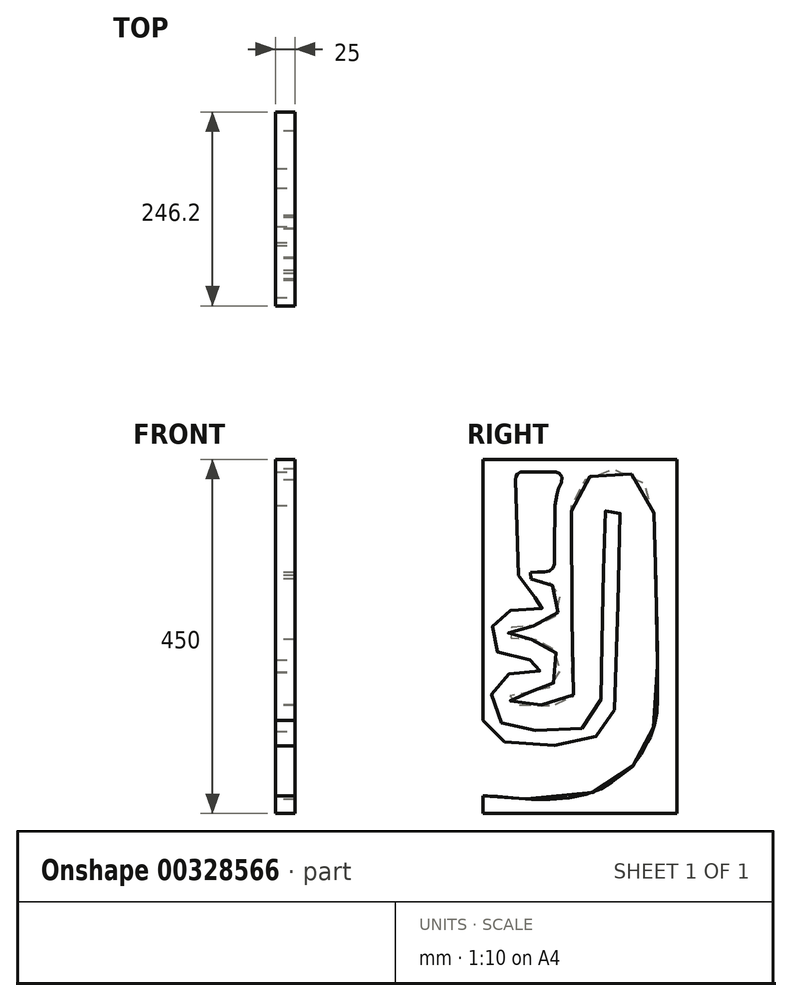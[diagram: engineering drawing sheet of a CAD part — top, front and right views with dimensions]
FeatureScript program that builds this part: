
annotation { "Feature Type Name" : "Feature", "Feature Type Description" : "" }
export const myFeature = defineFeature(function(context is Context, id is Id, definition is map)
    precondition{}
    {
        {
            var Q0;
            Q0=qCreatedBy(makeId("Right.planeOp"),FACE);
            var sketch = newSketch(context, id + "F0", { "sketchPlane" : qUnion([Q0])});
            skLineSegment(sketch, "E0", {"start": v(44.97, 302.71) * mm, "end": v(0, 299.98) * mm, "construction": true});
            skFitSpline(sketch, "E1", {"points": [v(44.97, 302.71) * mm, v(46.66, 291.94) * mm, v(50.27, 282.54) * mm, v(59.09, 276.03) * mm, v(68.36, 274.38) * mm, v(74.74, 273.73) * mm, v(78.42, 272.02) * mm, v(80.26, 269.38) * mm, v(80.2, 264.65) * mm, v(77.17, 261.43) * mm, v(68.75, 259.72) * mm, v(55.07, 259.45) * mm, v(46, 259.06) * mm, v(35.34, 258.27) * mm, v(29.89, 255.84) * mm, v(24.16, 251.82) * mm, v(20.48, 249.32) * mm, v(15.02, 242.35) * mm, v(11, 235.58) * mm, v(10.48, 227.42) * mm, v(11.27, 221.77) * mm, v(13.97, 212.36) * mm, v(17.78, 206.18) * mm, v(26.47, 199.14) * mm, v(35.8, 195.46) * mm, v(53.17, 195.06) * mm, v(64.61, 195) * mm, v(70.8, 195.06) * mm, v(75.4, 191.71) * mm, v(76.71, 186.98) * mm, v(74.87, 182.5) * mm, v(67.77, 179.87) * mm, v(54.09, 179.67) * mm, v(43.43, 180.07) * mm, v(35.21, 178.5) * mm, v(28.44, 175.47) * mm, v(22.26, 171.98) * mm, v(16.86, 164.68) * mm, v(12.32, 154.81) * mm, v(10.35, 147.32) * mm, v(11.54, 136.14) * mm, v(15.61, 125.09) * mm, v(22.32, 116.6) * mm, v(31.73, 109.9) * mm, v(40.87, 106.93) * mm, v(58.89, 105.55) * mm, v(77.96, 105.16) * mm, v(110.85, 104.76) * mm, v(124.86, 107.85) * mm, v(139.92, 120.28) * mm, v(146.03, 130.68) * mm, v(149.2, 139.82) * mm, v(149.65, 158.04) * mm, v(150.18, 193.82) * mm, v(151.82, 247.61) * mm, v(153.14, 301.35) * mm, v(154.98, 372.58) * mm, v(155.64, 381.32) * mm, v(156.3, 385.67) * mm, v(159.45, 388.89) * mm, v(163.53, 391.06) * mm, v(168.33, 390.27) * mm, v(171.82, 387.7) * mm, v(173.79, 384.48) * mm, v(174.05, 374.22) * mm, v(173.79, 364.03) * mm, v(168.9, 144.4) * mm, v(167.8, 134) * mm, v(164.37, 124.81) * mm, v(159.61, 114.2) * mm, v(151.43, 104.8) * mm, v(141.58, 96.94) * mm, v(125, 88.75) * mm, v(106.85, 86.2) * mm, v(74.11, 86.76) * mm, v(39.6, 88.1) * mm, v(27.76, 90.97) * mm, v(15.7, 99.15) * mm, v(5.53, 109.1) * mm, v(1.86, 114.4) * mm, v(0, 118.29) * mm], "startDerivative": vector(122.26, -918.43) * mm, "endDerivative": vector(-644.26, 1390.33) * mm});
            skLineSegment(sketch, "E2", {"start": v(0, 299.98) * mm, "end": v(0, 118.29) * mm});
            skLineSegment(sketch, "E3", {"start": v(60.06, 306.23) * mm, "end": v(61.1, 297.88) * mm});
            skFitSpline(sketch, "E4", {"points": [v(61.1, 297.88) * mm, v(72.73, 298.12) * mm, v(76.22, 297.67) * mm, v(82.27, 294.66) * mm, v(85.78, 292.32) * mm, v(89.7, 288.19) * mm, v(96.14, 279.22) * mm, v(97.79, 271.55) * mm, v(96.14, 257.9) * mm, v(91.8, 251.04) * mm, v(86.54, 245.88) * mm, v(76.7, 240.73) * mm, v(63.86, 238.27) * mm, v(43.23, 237.86) * mm, v(36.85, 236.86) * mm, v(33.74, 234.05) * mm, v(32.16, 229.54) * mm, v(33.16, 225.67) * mm, v(33.57, 224.85) * mm, v(37.26, 221.98) * mm, v(50.68, 221.22) * mm, v(65.56, 221.33) * mm, v(75.75, 219.28) * mm, v(85.07, 213.9) * mm, v(91.57, 206.4) * mm, v(96.55, 196.37) * mm, v(97.84, 183.48) * mm, v(93.21, 170.12) * mm, v(86.89, 162.97) * mm, v(82.73, 159.22) * mm, v(76.75, 155.47) * mm, v(65.5, 154.3) * mm, v(48.8, 153.72) * mm, v(39.54, 152.84) * mm, v(35.8, 151.08) * mm, v(33.86, 148.33) * mm, v(34.62, 142.88) * mm, v(36.85, 139.65) * mm, v(42.3, 137.95) * mm, v(52.32, 138.13) * mm, v(85.95, 137.6) * mm, v(105.34, 137.95) * mm, v(113.6, 144.46) * mm, v(114.54, 155.83) * mm, v(113.2, 177.39) * mm, v(113.17, 366.49) * mm, v(112.47, 390.86) * mm, v(119.73, 412.66) * mm, v(134.03, 426.96) * mm, v(150.44, 435.4) * mm, v(174.81, 436.33) * mm, v(199.66, 423.67) * mm, v(213.02, 406.33) * mm, v(217.7, 369.07) * mm, v(219.1, 302.74) * mm, v(220.98, 246.96) * mm, v(221.92, 147.35) * mm, v(219.81, 120.4) * mm, v(211.84, 96.02) * mm, v(210.2, 92.74) * mm, v(193.1, 63.44) * mm, v(171.53, 45.63) * mm, v(148.8, 30.63) * mm, v(102.86, 18.9) * mm, v(44.26, 19.38) * mm, v(8.87, 22.19) * mm, v(3.48, 22.12) * mm, v(0, 22.38) * mm], "startDerivative": vector(1053.99, 27.4) * mm, "endDerivative": vector(-1143.94, 83.98) * mm});
            skFitSpline(sketch, "E5", {"points": [v(60.06, 306.23) * mm, v(72.98, 306.87) * mm, v(82.66, 307.61) * mm, v(86.85, 309.63) * mm, v(89.86, 313.94) * mm, v(90.7, 321.24) * mm, v(91.57, 387.21) * mm, v(92.4, 397.8) * mm, v(93.94, 406.03) * mm, v(97.28, 415.64) * mm, v(100.63, 424.42) * mm, v(99.37, 430) * mm, v(96.03, 432.79) * mm, v(91.43, 433.76) * mm, v(81.12, 433.76) * mm, v(50.18, 433.9) * mm, v(45.58, 432.93) * mm, v(43.8, 431.4) * mm, v(42.5, 429.05) * mm, v(42.12, 427.92) * mm, v(41.18, 423.54) * mm], "startDerivative": vector(213.16, 11.68) * mm, "endDerivative": vector(-55, -245.9) * mm});
            skLineSegment(sketch, "E6", {"start": v(41.18, 423.54) * mm, "end": v(0, 424.22) * mm, "construction": true});
            skLineSegment(sketch, "E7", {"start": v(0, 424.22) * mm, "end": v(0, 450) * mm});
            skLineSegment(sketch, "E8", {"start": v(0, 450) * mm, "end": v(246.2, 450) * mm});
            skLineSegment(sketch, "E9", {"start": v(246.2, 450) * mm, "end": v(246.2, 0) * mm});
            skLineSegment(sketch, "E10", {"start": v(246.2, 0) * mm, "end": v(0, 0) * mm});
            skLineSegment(sketch, "E11", {"start": v(0, 0) * mm, "end": v(0, 22.38) * mm});
            skLineSegment(sketch, "E12", {"start": v(0, 424.22) * mm, "end": v(0, 299.98) * mm});
            skLineSegment(sketch, "E13", {"start": v(44.97, 302.71) * mm, "end": v(41.18, 423.54) * mm});
            skSolve(sketch);
        }
        {
            var Q0;
            Q0=makeQuery(id+"F0.imprint","IMPRINT",FACE,{"disambiguationData":[TD([[makeQuery(id+"F0.imprint","IMPRINT",EDGE,{"derivedFrom":sQuery(id+"F0.wireOp",EDGE,"E1")}),-1.0]])]});
            extrude(context, id + "F1", {"entities" : qUnion([Q0]), "depth" : 25 * mm});
        }
    });
